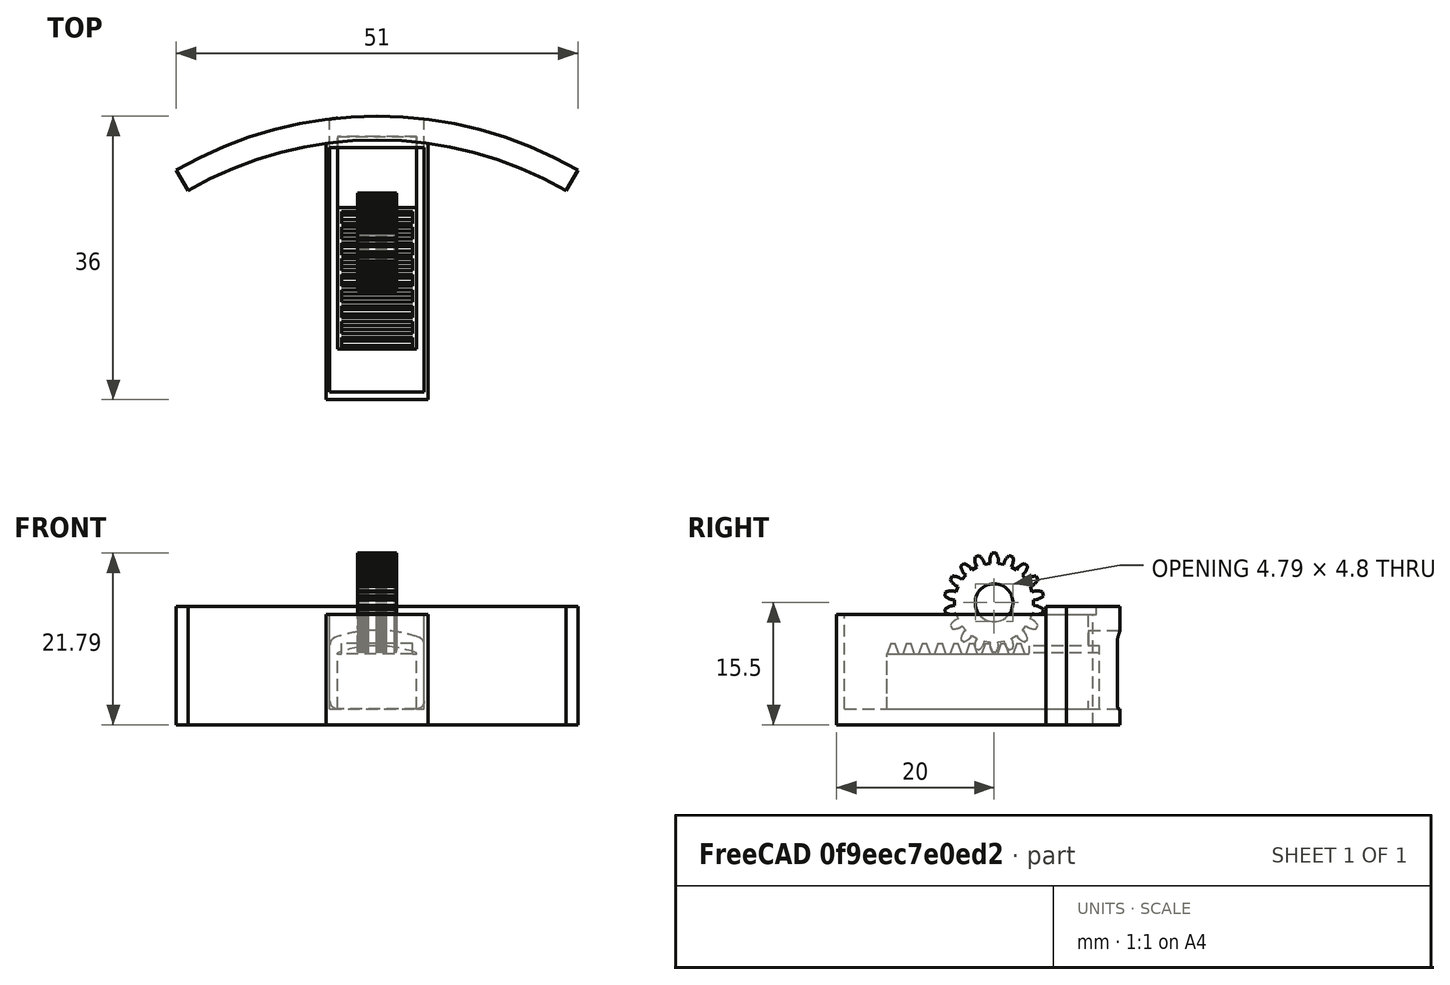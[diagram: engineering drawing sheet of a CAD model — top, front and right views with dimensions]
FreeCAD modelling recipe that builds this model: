
FCSTD DOCUMENT  (FreeCAD 0.16R4924 (Git))
Label: interior_servo_bay_v4p10
License: All rights reserved
LicenseURL: http://en.wikipedia.org/wiki/All_rights_reserved
objects: Part::Feature×11, Part::Cut×5, Part::Box×5, Part::MultiFuse×4, Part::Cylinder×3, Part::Extrusion×3, Part::Thickness×1, Mesh::Feature×1, Part::Fuse×1, Part::FeaturePython×1, Part::Prism×1, Part::MultiCommon×1
note: 36 computed .brp shape members not serialized (recipe doc carries the construction recipe); baked Part::Feature solids carry a one-line shape summary decoded from their .brp

FEATURE [Part::Cylinder] Cylinder  label="bottle_wall"
  Angle = 60
  Height = 15
  Placement = pos=(8.5,-7,0) rot=(0,0,1;1.0472rad)
  Radius = 51
FEATURE [Part::Cylinder] Cylinder001  label="bottle_wall001"
  Angle = 60
  Height = 15
  Placement = pos=(8.5,-7,0) rot=(0,0,1;1.0472rad)
  Radius = 48
FEATURE [Part::Cut] Cut  label="bottle_wall_composite"
  Base = -> Cylinder
  Placement = pos=(0,-2,0) rot=(0,0,1;0rad)
  Tool = -> Cylinder001
FEATURE [Part::Feature] Common_cs  label="pin_cs"
  Placement = pos=(3.5,35,2) rot=(0,0,1;0rad)
  shape: bbox 10 x 2e-07 x 8 mm, 0 faces, 0 solids (baked)
FEATURE [Part::Extrusion] Extrude
  Base = -> Common_cs
  Dir = (0,5,0)
  Solid = true
FEATURE [Part::Thickness] Thickness
  Faces = -> Extrude [Face7]
  Intersection = false
  Join = 0
  Mode = 0
  SelfIntersection = false
  Value = 1
FEATURE [Part::Feature] Common_cs001  label="pin_cs001"
  Placement = pos=(3.5,35,2) rot=(0,0,1;0rad)
  shape: bbox 10 x 2e-07 x 8 mm, 0 faces, 0 solids (baked)
FEATURE [Part::Extrusion] Extrude001
  Base = -> Common_cs001
  Dir = (0,5,0)
  Solid = true
FEATURE [Part::MultiFuse] Fusion  label="bolt_bottle_side_opening"
  Placement = pos=(0,-7,1) rot=(0,0,1;0rad)
  Shapes = -> [Thickness,Extrude,Extrude001]
FEATURE [Part::Box] Box  label="pullBay"
  Height = 15
  Length = 12
  Placement = pos=(2.5,7,2) rot=(0,0,1;0rad)
  Width = 31
FEATURE [Part::Box] Box001  label="Case"
  Height = 14
  Length = 13
  Placement = pos=(2,6,0) rot=(0,0,1;0rad)
  Width = 34
FEATURE [Part::Cut] Cut001  label="cut bay from case"
  Base = -> Box001
  Tool = -> Box
FEATURE [Part::MultiFuse] Fusion001  label="wall plus case"
  Shapes = -> [Cut,Cut001]
FEATURE [Part::Cut] Cut002  label="hole cut out of case"
  Base = -> Fusion001
  Tool = -> Fusion
FEATURE [Mesh::Feature] Mesh  label="servo_motor_2"
  Placement = pos=(33.6,-52,22) rot=(0,0,-1;1.5708rad)
FEATURE [Part::Fuse] union  label="pinion"
FEATURE [Part::FeaturePython] RefineLinearExtrude  # WARN: FeaturePython — macro-defined, semantics opaque (R4)
  Base = -> union
FEATURE [Part::Extrusion] LinearExtrude
  Base = -> RefineLinearExtrude
  Dir = (0,0,5)
  Solid = true
FEATURE [Part::Prism] prism
  Circumradius = 2.4
  Height = 7
  Placement = pos=(0,0,-1) rot=(0,0,1;0rad)
  Polygon = 50
FEATURE [Part::Cut] difference  label="pinion_final"
  Base = -> LinearExtrude
  Placement = pos=(6,26,15.5) rot=(0,1,0;1.5708rad)
  Tool = -> prism
FEATURE [Part::Cylinder] Cylinder002  label="rounded_top"
  Angle = 360
  Height = 40
  Placement = pos=(5,35,-7) rot=(1,0,0;1.5708rad)
  Radius = 15
FEATURE [Part::Box] Box005  label="pin"
  Height = 8
  Length = 10
  Width = 27
FEATURE [Part::MultiCommon] Common  label="rounded pin"
  Shapes = -> [Cylinder002,Box005]
FEATURE [Part::Box] Box006  label="flat_top"
  Height = 10
  Length = 10
  Placement = pos=(0,0,7) rot=(0,0,1;0rad)
  Width = 18
FEATURE [Part::Cut] Cut005
  Base = -> Common
  Placement = pos=(0,11,0) rot=(0,0,1;0rad)
  Tool = -> Box006
FEATURE [Part::Box] cube
  Height = 5
  Length = 18
  Placement = pos=(-12,-4.5,-2.5) rot=(0,0,1;0rad)
  Width = 9
FEATURE [Part::Feature] polyhedron
  Placement = pos=(-11.2451,0,2.5) rot=(0,0,1;0rad)
  shape: bbox 1.51 x 9 x 1.337 mm, 6 faces (baked)
FEATURE [Part::Feature] polyhedron001
  Placement = pos=(-9.24512,0,2.5) rot=(0,0,1;0rad)
  shape: bbox 1.51 x 9 x 1.337 mm, 6 faces (baked)
FEATURE [Part::Feature] polyhedron002
  Placement = pos=(-7.24512,0,2.5) rot=(0,0,1;0rad)
  shape: bbox 1.51 x 9 x 1.337 mm, 6 faces (baked)
FEATURE [Part::Feature] polyhedron003
  Placement = pos=(-5.24512,0,2.5) rot=(0,0,1;0rad)
  shape: bbox 1.51 x 9 x 1.337 mm, 6 faces (baked)
FEATURE [Part::Feature] polyhedron004
  Placement = pos=(-3.24512,0,2.5) rot=(0,0,1;0rad)
  shape: bbox 1.51 x 9 x 1.337 mm, 6 faces (baked)
FEATURE [Part::Feature] polyhedron005
  Placement = pos=(-1.24512,0,2.5) rot=(0,0,1;0rad)
  shape: bbox 1.51 x 9 x 1.337 mm, 6 faces (baked)
FEATURE [Part::Feature] polyhedron006
  Placement = pos=(0.754882,0,2.5) rot=(0,0,1;0rad)
  shape: bbox 1.51 x 9 x 1.337 mm, 6 faces (baked)
FEATURE [Part::Feature] polyhedron007
  Placement = pos=(2.75488,0,2.5) rot=(0,0,1;0rad)
  shape: bbox 1.51 x 9 x 1.337 mm, 6 faces (baked)
FEATURE [Part::Feature] polyhedron008
  Placement = pos=(4.75488,0,2.5) rot=(0,0,1;0rad)
  shape: bbox 1.51 x 9 x 1.337 mm, 6 faces (baked)
FEATURE [Part::MultiFuse] Fusion003  label="rack"
  Placement = pos=(5,23,4.5) rot=(0,0,1;1.5708rad)
  Shapes = -> [cube,polyhedron002,polyhedron003,polyhedron004,polyhedron005,polyhedron,polyhedron007,polyhedron001,polyhedron006,polyhedron008]
FEATURE [Part::MultiFuse] Fusion004  label="pin_3p2"
  Placement = pos=(3.5,1.4,2) rot=(0,0,1;0rad)
  Shapes = -> [Fusion003,Cut005]
